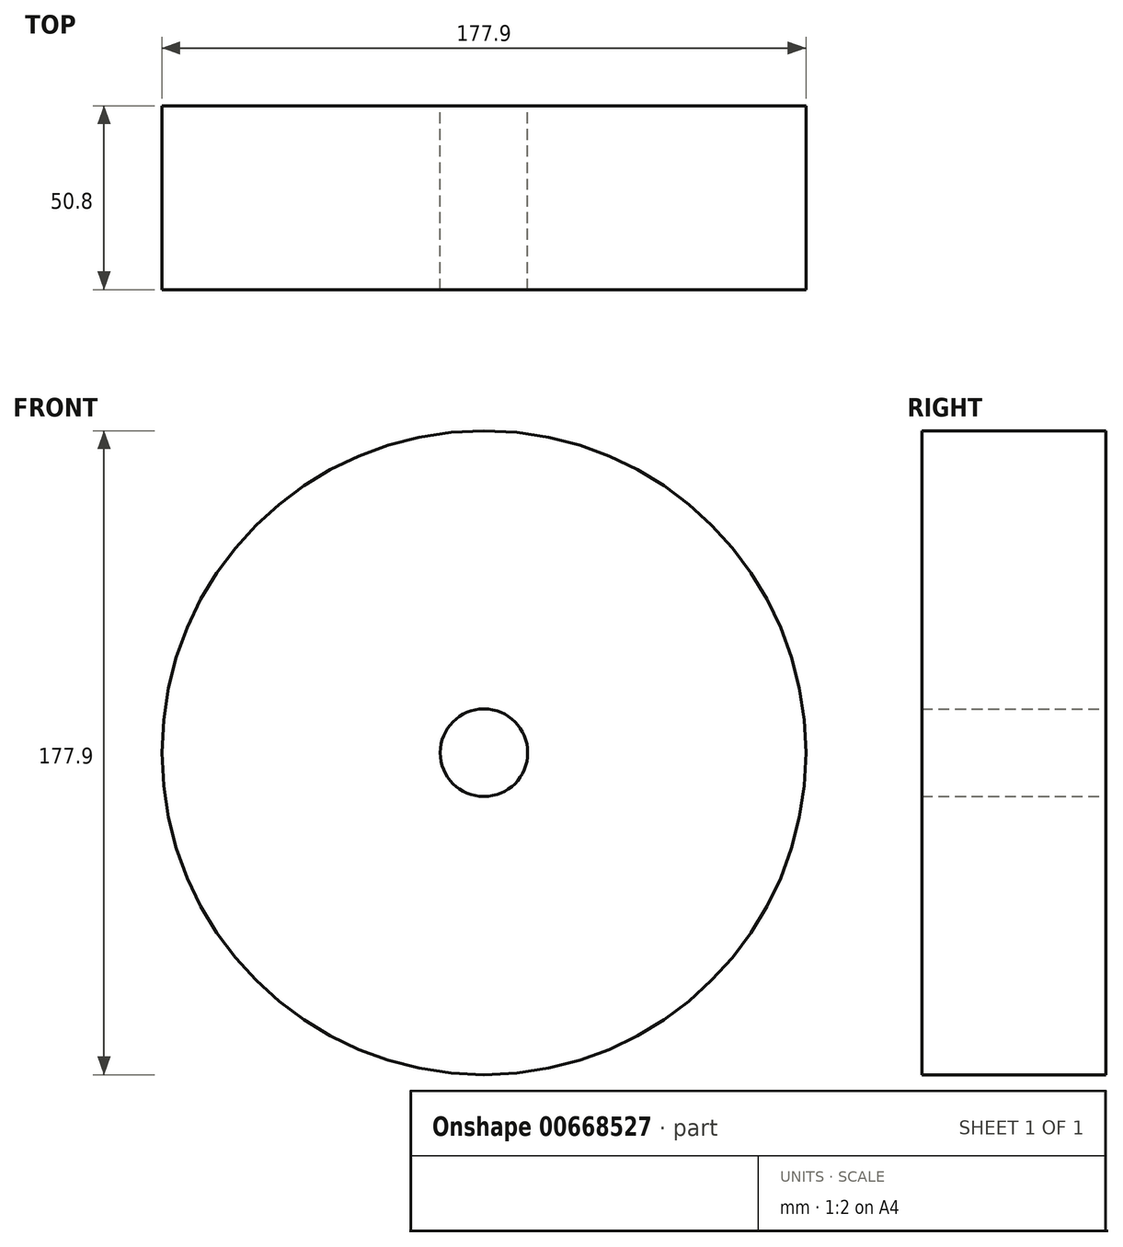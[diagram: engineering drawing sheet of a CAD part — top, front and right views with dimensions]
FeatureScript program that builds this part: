
annotation { "Feature Type Name" : "Feature", "Feature Type Description" : "" }
export const myFeature = defineFeature(function(context is Context, id is Id, definition is map)
    precondition{}
    {
        {
            var Q0;
            Q0=qCreatedBy(makeId("Front.planeOp"),FACE);
            var sketch = newSketch(context, id + "F0", { "sketchPlane" : qUnion([Q0])});
            skCircle(sketch, "E0", {"center": v(0, 0) * mm, "radius": 88.95 * mm});
            skCircle(sketch, "E1", {"center": v(0, 0) * mm, "radius": 12.09 * mm});
            skSolve(sketch);
        }
        {
            var Q0;
            Q0 = qSketchRegion(id + "F0", true);
            extrude(context, id + "F1", {"entities" : qUnion([Q0]), "depth" : 50.8 * mm, "offsetDistance" : 25.4 * mm});
        }
    });
